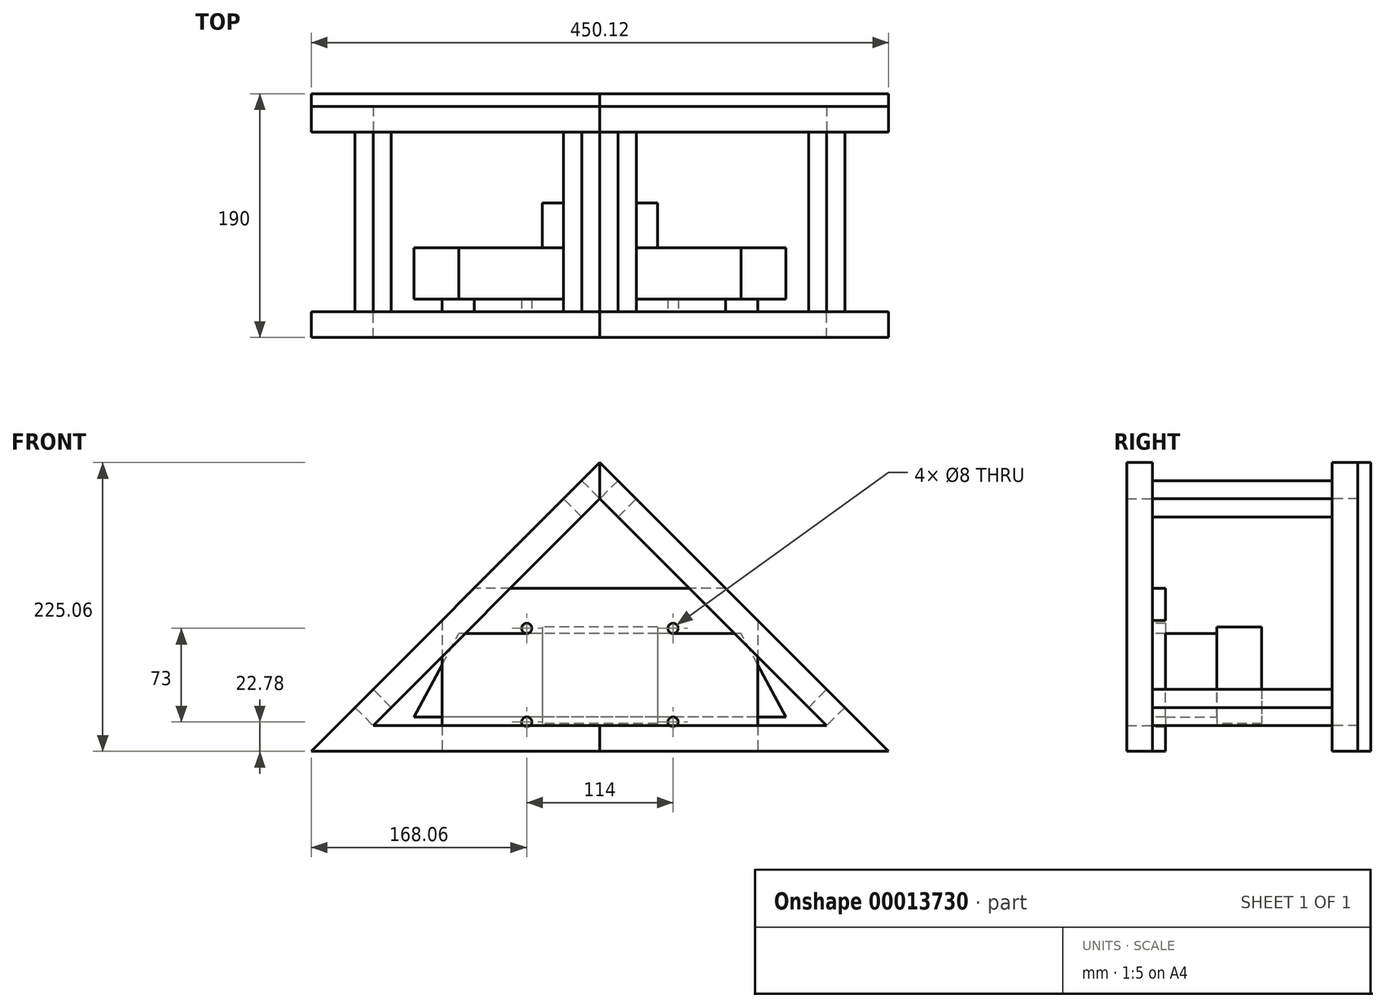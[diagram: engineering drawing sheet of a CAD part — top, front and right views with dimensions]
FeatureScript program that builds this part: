
annotation { "Feature Type Name" : "Feature", "Feature Type Description" : "" }
export const myFeature = defineFeature(function(context is Context, id is Id, definition is map)
    precondition{}
    {
        {
            var Q0;
            Q0=qCreatedBy(makeId("Front.planeOp"),FACE);
            var sketch = newSketch(context, id + "F0", { "sketchPlane" : qUnion([Q0])});
            skLineSegment(sketch, "E0", {"start": v(0, 0) * mm, "end": v(-145, 0) * mm});
            skLineSegment(sketch, "E1", {"start": v(-145, 0) * mm, "end": v(-110, 65) * mm});
            skLineSegment(sketch, "E2", {"start": v(-110, 65) * mm, "end": v(0, 65) * mm});
            skLineSegment(sketch, "E3", {"start": v(0, 65) * mm, "end": v(0, 0) * mm, "construction": true});
            skLineSegment(sketch, "E4.0.MirrorCS", {"start": v(110, 65) * mm, "end": v(0, 65) * mm});
            skLineSegment(sketch, "E5.0.MirrorCS", {"start": v(145, 0) * mm, "end": v(110, 65) * mm});
            skLineSegment(sketch, "E6.0.MirrorCS", {"start": v(0, 0) * mm, "end": v(145, 0) * mm});
            skSolve(sketch);
        }
        {
            var Q0;
            Q0 = qSketchRegion(id + "F0", true);
            extrude(context, id + "F1", {"entities" : qUnion([Q0]), "depth" : 40 * mm});
        }
        {
            var Q0;
            Q0=qCreatedBy(makeId("Front.planeOp"),FACE);
            var sketch = newSketch(context, id + "F2", { "sketchPlane" : qUnion([Q0])});
            skLineSegment(sketch, "E7.bottom", {"start": v(45, 70) * mm, "end": v(-45, 70) * mm});
            skLineSegment(sketch, "E7.top", {"start": v(45, -5) * mm, "end": v(-45, -5) * mm});
            skLineSegment(sketch, "E7.left", {"start": v(45, 70) * mm, "end": v(45, -5) * mm});
            skLineSegment(sketch, "E7.right", {"start": v(-45, 70) * mm, "end": v(-45, -5) * mm});
            skSolve(sketch);
        }
        {
            var Q0;
            Q0 = qSketchRegion(id + "F2", true);
            extrude(context, id + "F3", {"entities" : qUnion([Q0]), "operationType" : NewBodyOperationType.ADD, "oppositeDirection" : true, "depth" : 35 * mm});
        }
        {
            var Q0;
            Q0=qCreatedBy(makeId("Front.planeOp"),FACE);
            var sketch = newSketch(context, id + "F4", { "sketchPlane" : qUnion([Q0])});
            skLineSegment(sketch, "E8", {"start": v(0, -182.57) * mm, "end": v(0, 158.85) * mm, "construction": true});
            skLineSegment(sketch, "E9", {"start": v(0, 170) * mm, "end": v(-176.78, -6.78) * mm});
            skLineSegment(sketch, "E10", {"start": v(-14.14, 184.14) * mm, "end": v(-190.92, 7.37) * mm});
            skLineSegment(sketch, "E11", {"start": v(0, 170) * mm, "end": v(-14.14, 184.14) * mm});
            skLineSegment(sketch, "E12", {"start": v(-176.78, -6.78) * mm, "end": v(-190.92, 7.37) * mm});
            skLineSegment(sketch, "E13.bottom", {"start": v(-176.78, -6.78) * mm, "end": v(0, -6.78) * mm});
            skLineSegment(sketch, "E13.top", {"start": v(-176.78, -26.78) * mm, "end": v(0, -26.78) * mm});
            skLineSegment(sketch, "E13.left", {"start": v(-176.78, -6.78) * mm, "end": v(-176.78, -26.78) * mm});
            skLineSegment(sketch, "E13.right", {"start": v(0, -6.78) * mm, "end": v(0, -26.78) * mm});
            skLineSegment(sketch, "E14", {"start": v(-176.78, -26.78) * mm, "end": v(-225.06, -26.78) * mm});
            skLineSegment(sketch, "E15", {"start": v(-225.06, -26.78) * mm, "end": v(-190.92, 7.37) * mm});
            skLineSegment(sketch, "E16", {"start": v(-225.06, -26.78) * mm, "end": v(-176.78, -6.78) * mm});
            skLineSegment(sketch, "E17", {"start": v(-14.14, 184.14) * mm, "end": v(0, 198.28) * mm});
            skLineSegment(sketch, "E18", {"start": v(0, 198.28) * mm, "end": v(0, 170) * mm});
            skSolve(sketch);
        }
        {
            var Q0;
            Q0 = qSketchRegion(id + "F4", true);
            extrude(context, id + "F5", {"entities" : qUnion([Q0]), "operationType" : NewBodyOperationType.ADD, "oppositeDirection" : true, "depth" : 110 * mm, "hasSecondDirection" : true, "secondDirectionOppositeDirection" : true, "secondDirectionDepth" : 90 * mm});
        }
        {
            var Q0;
            Q0=makeQuery(id+"F1.opExtrude","CAP_FACE",FACE,{"disambiguationData":[OSD([sQuery(id+"F0.wireOp",EDGE,"E0"),sQuery(id+"F0.wireOp",EDGE,"E1"),sQuery(id+"F0.wireOp",EDGE,"E2"),sQuery(id+"F0.wireOp",EDGE,"E4.0.MirrorCS"),sQuery(id+"F0.wireOp",EDGE,"E5.0.MirrorCS"),sQuery(id+"F0.wireOp",EDGE,"E6.0.MirrorCS")])],"isStart":false});
            cPlane(context, id + "F6", {"entities" : qUnion([Q0]), "cplaneType" : CPlaneType.OFFSET, "offset" : 10 * mm, "width" : 150 * mm, "height" : 150 * mm});
        }
        {
            var Q0;
            Q0=qCreatedBy(id+"F6.planeOp",FACE);
            var sketch = newSketch(context, id + "F7", { "sketchPlane" : qUnion([Q0])});
            skLineSegment(sketch, "E19", {"start": v(0, -115.22) * mm, "end": v(0, 226.2) * mm, "construction": true});
            skLineSegment(sketch, "E20", {"start": v(0, 170) * mm, "end": v(-176.78, -6.78) * mm});
            skLineSegment(sketch, "E21", {"start": v(-14.14, 184.14) * mm, "end": v(-190.92, 7.37) * mm});
            skLineSegment(sketch, "E22", {"start": v(0, 170) * mm, "end": v(-14.14, 184.14) * mm});
            skLineSegment(sketch, "E23", {"start": v(-176.78, -6.78) * mm, "end": v(-190.92, 7.37) * mm});
            skLineSegment(sketch, "E24.bottom", {"start": v(-176.78, -6.78) * mm, "end": v(0, -6.78) * mm});
            skLineSegment(sketch, "E24.top", {"start": v(-176.78, -26.78) * mm, "end": v(0, -26.78) * mm});
            skLineSegment(sketch, "E24.left", {"start": v(-176.78, -6.78) * mm, "end": v(-176.78, -26.78) * mm});
            skLineSegment(sketch, "E24.right", {"start": v(0, -6.78) * mm, "end": v(0, -26.78) * mm});
            skLineSegment(sketch, "E25", {"start": v(-176.78, -26.78) * mm, "end": v(-225.06, -26.78) * mm});
            skLineSegment(sketch, "E26", {"start": v(-225.06, -26.78) * mm, "end": v(-190.92, 7.37) * mm});
            skLineSegment(sketch, "E27", {"start": v(-225.06, -26.78) * mm, "end": v(-176.78, -6.78) * mm});
            skLineSegment(sketch, "E28", {"start": v(-14.14, 184.14) * mm, "end": v(0, 198.28) * mm});
            skLineSegment(sketch, "E29", {"start": v(0, 198.28) * mm, "end": v(0, 170) * mm});
            skSolve(sketch);
        }
        {
            var Q0;
            Q0 = qSketchRegion(id + "F7", true);
            extrude(context, id + "F8", {"entities" : qUnion([Q0]), "operationType" : NewBodyOperationType.ADD, "depth" : 20 * mm});
        }
        {
            var Q0;
            Q0=makeQuery(id+"F8.opExtrude","SWEPT_BODY",BODY,{"disambiguationData":[OSD([sQuery(id+"F7.wireOp",EDGE,"E20"),sQuery(id+"F7.wireOp",EDGE,"E21"),sQuery(id+"F7.wireOp",EDGE,"E24.bottom"),sQuery(id+"F7.wireOp",EDGE,"E24.top"),sQuery(id+"F7.wireOp",EDGE,"E24.right"),sQuery(id+"F7.wireOp",EDGE,"E25"),sQuery(id+"F7.wireOp",EDGE,"E26"),sQuery(id+"F7.wireOp",EDGE,"E28"),sQuery(id+"F7.wireOp",EDGE,"E29")])]});
            var Q1;
            Q1=makeQuery(id+"F5.opExtrude","SWEPT_BODY",BODY,{"disambiguationData":[OSD([sQuery(id+"F4.wireOp",EDGE,"E9"),sQuery(id+"F4.wireOp",EDGE,"E10"),sQuery(id+"F4.wireOp",EDGE,"E13.bottom"),sQuery(id+"F4.wireOp",EDGE,"E13.top"),sQuery(id+"F4.wireOp",EDGE,"E13.right"),sQuery(id+"F4.wireOp",EDGE,"E14"),sQuery(id+"F4.wireOp",EDGE,"E15"),sQuery(id+"F4.wireOp",EDGE,"E17"),sQuery(id+"F4.wireOp",EDGE,"E18")])]});
            var Q2;
            Q2=qCreatedBy(makeId("Right.planeOp"),FACE);
            mirror(context, id + "F9", {"operationType" : NewBodyOperationType.ADD, "entities" : qUnion([Q0, Q1]), "mirrorPlane" : qUnion([Q2])});
        }
        {
            var Q0;
            {var subQ0=makeQuery(id+"F8.opExtrude","CAP_FACE",FACE,{"disambiguationData":[OSD([sQuery(id+"F7.wireOp",EDGE,"E20"),sQuery(id+"F7.wireOp",EDGE,"E21"),sQuery(id+"F7.wireOp",EDGE,"E24.bottom"),sQuery(id+"F7.wireOp",EDGE,"E24.top"),sQuery(id+"F7.wireOp",EDGE,"E24.right"),sQuery(id+"F7.wireOp",EDGE,"E25"),sQuery(id+"F7.wireOp",EDGE,"E26"),sQuery(id+"F7.wireOp",EDGE,"E28"),sQuery(id+"F7.wireOp",EDGE,"E29")])],"isStart":true});Q0=makeQuery(id+"F9.boolean.opBoolean","MERGE",FACE,{"derivedFrom":[subQ0,makeQuery(id+"F9.opPattern","COPY",FACE,{"derivedFrom":subQ0,"instanceName":"1"})]});}
            var sketch = newSketch(context, id + "F10", { "sketchPlane" : qUnion([Q0])});
            skLineSegment(sketch, "E30", {"start": v(-98.05, 100.23) * mm, "end": v(-123.08, 75.2) * mm});
            skLineSegment(sketch, "E31", {"start": v(-123.08, -26.78) * mm, "end": v(123.08, -26.78) * mm});
            skLineSegment(sketch, "E32", {"start": v(123.08, 75.2) * mm, "end": v(98.05, 100.23) * mm});
            skLineSegment(sketch, "E33", {"start": v(0, 198.28) * mm, "end": v(0, 32.3) * mm, "construction": true});
            skCircle(sketch, "E34", {"center": v(-57, 69) * mm, "radius": 4 * mm});
            skCircle(sketch, "E35.0.MirrorC", {"center": v(57, 69) * mm, "radius": 4 * mm});
            skCircle(sketch, "E36", {"center": v(-57, -4) * mm, "radius": 4 * mm});
            skCircle(sketch, "E37.0.MirrorC", {"center": v(57, -4) * mm, "radius": 4 * mm});
            skLineSegment(sketch, "E38", {"start": v(-98.05, 100.23) * mm, "end": v(98.05, 100.23) * mm});
            skLineSegment(sketch, "E39", {"start": v(-123.08, 75.2) * mm, "end": v(-123.08, -26.78) * mm});
            skLineSegment(sketch, "E40.0.MirrorCS", {"start": v(123.08, 75.2) * mm, "end": v(123.08, -26.78) * mm});
            skSolve(sketch);
        }
        {
            var Q0;
            Q0 = qSketchRegion(id + "F10", true);
            extrude(context, id + "F11", {"entities" : qUnion([Q0]), "depth" : 10 * mm});
        }
        {
            var Q0;
            {var subQ0=makeQuery(id+"F5.opExtrude","CAP_FACE",FACE,{"disambiguationData":[OSD([sQuery(id+"F4.wireOp",EDGE,"E9"),sQuery(id+"F4.wireOp",EDGE,"E10"),sQuery(id+"F4.wireOp",EDGE,"E13.bottom"),sQuery(id+"F4.wireOp",EDGE,"E13.top"),sQuery(id+"F4.wireOp",EDGE,"E13.right"),sQuery(id+"F4.wireOp",EDGE,"E14"),sQuery(id+"F4.wireOp",EDGE,"E15"),sQuery(id+"F4.wireOp",EDGE,"E17"),sQuery(id+"F4.wireOp",EDGE,"E18")])],"isStart":false});Q0=makeQuery(id+"F9.boolean.opBoolean","MERGE",FACE,{"derivedFrom":[subQ0,makeQuery(id+"F9.opPattern","COPY",FACE,{"derivedFrom":subQ0,"instanceName":"1"})]});}
            var sketch = newSketch(context, id + "F12", { "sketchPlane" : qUnion([Q0])});
            skLineSegment(sketch, "E41", {"start": v(0, 198.28) * mm, "end": v(-225.06, -26.78) * mm});
            skLineSegment(sketch, "E42", {"start": v(-225.06, -26.78) * mm, "end": v(225.06, -26.78) * mm});
            skLineSegment(sketch, "E43", {"start": v(225.06, -26.78) * mm, "end": v(0, 198.28) * mm});
            skSolve(sketch);
        }
        {
            var Q0;
            Q0 = qSketchRegion(id + "F12", true);
            extrude(context, id + "F13", {"entities" : qUnion([Q0]), "depth" : 10 * mm});
        }
        {
            var Q0;
            {var subQ0=makeQuery(id+"F8.opExtrude","CAP_FACE",FACE,{"disambiguationData":[OSD([sQuery(id+"F7.wireOp",EDGE,"E20"),sQuery(id+"F7.wireOp",EDGE,"E21"),sQuery(id+"F7.wireOp",EDGE,"E24.bottom"),sQuery(id+"F7.wireOp",EDGE,"E24.top"),sQuery(id+"F7.wireOp",EDGE,"E24.right"),sQuery(id+"F7.wireOp",EDGE,"E25"),sQuery(id+"F7.wireOp",EDGE,"E26"),sQuery(id+"F7.wireOp",EDGE,"E28"),sQuery(id+"F7.wireOp",EDGE,"E29")])],"isStart":true});Q0=makeQuery(id+"F9.boolean.opBoolean","MERGE",FACE,{"derivedFrom":[subQ0,makeQuery(id+"F9.opPattern","COPY",FACE,{"derivedFrom":subQ0,"instanceName":"1"})]});}
            var sketch = newSketch(context, id + "F14", { "sketchPlane" : qUnion([Q0])});
            skLineSegment(sketch, "E44", {"start": v(0, 170) * mm, "end": v(-14.14, 184.14) * mm});
            skLineSegment(sketch, "E45", {"start": v(-14.14, 184.14) * mm, "end": v(-28.28, 170) * mm});
            skLineSegment(sketch, "E46", {"start": v(-28.28, 170) * mm, "end": v(-14.14, 155.86) * mm});
            skLineSegment(sketch, "E47", {"start": v(-14.14, 155.86) * mm, "end": v(0, 170) * mm});
            skLineSegment(sketch, "E48", {"start": v(-176.78, -6.78) * mm, "end": v(-190.92, 7.37) * mm});
            skLineSegment(sketch, "E49", {"start": v(-190.92, 7.37) * mm, "end": v(-176.78, 21.5) * mm});
            skLineSegment(sketch, "E50", {"start": v(-176.78, 21.5) * mm, "end": v(-162.63, 7.37) * mm});
            skLineSegment(sketch, "E51", {"start": v(-162.63, 7.37) * mm, "end": v(-176.78, -6.78) * mm});
            skLineSegment(sketch, "E52", {"start": v(0, 198.28) * mm, "end": v(0, 145.24) * mm, "construction": true});
            skLineSegment(sketch, "E53.0.MirrorCS", {"start": v(0, 170) * mm, "end": v(14.14, 184.14) * mm});
            skLineSegment(sketch, "E54.0.MirrorCS", {"start": v(14.14, 184.14) * mm, "end": v(28.28, 170) * mm});
            skLineSegment(sketch, "E55.0.MirrorCS", {"start": v(28.28, 170) * mm, "end": v(14.14, 155.86) * mm});
            skLineSegment(sketch, "E56.0.MirrorCS", {"start": v(14.14, 155.86) * mm, "end": v(0, 170) * mm});
            skLineSegment(sketch, "E57.0.MirrorCS", {"start": v(190.92, 7.37) * mm, "end": v(176.78, 21.5) * mm});
            skLineSegment(sketch, "E58.0.MirrorCS", {"start": v(176.78, -6.78) * mm, "end": v(190.92, 7.37) * mm});
            skLineSegment(sketch, "E59.0.MirrorCS", {"start": v(176.78, 21.5) * mm, "end": v(162.63, 7.37) * mm});
            skLineSegment(sketch, "E60.0.MirrorCS", {"start": v(162.63, 7.37) * mm, "end": v(176.78, -6.78) * mm});
            skSolve(sketch);
        }
        {
            var Q0;
            Q0 = qSketchRegion(id + "F14", true);
            var Q1;
            {var subQ0=makeQuery(id+"F5.opExtrude","CAP_FACE",FACE,{"disambiguationData":[OSD([sQuery(id+"F4.wireOp",EDGE,"E9"),sQuery(id+"F4.wireOp",EDGE,"E10"),sQuery(id+"F4.wireOp",EDGE,"E13.bottom"),sQuery(id+"F4.wireOp",EDGE,"E13.top"),sQuery(id+"F4.wireOp",EDGE,"E13.right"),sQuery(id+"F4.wireOp",EDGE,"E14"),sQuery(id+"F4.wireOp",EDGE,"E15"),sQuery(id+"F4.wireOp",EDGE,"E17"),sQuery(id+"F4.wireOp",EDGE,"E18")])],"isStart":true});Q1=makeQuery(id+"F9.boolean.opBoolean","MERGE",FACE,{"derivedFrom":[subQ0,makeQuery(id+"F9.opPattern","COPY",FACE,{"derivedFrom":subQ0,"instanceName":"1"})]});}
            extrude(context, id + "F15", {"entities" : qUnion([Q0]), "endBound" : BoundingType.UP_TO_SURFACE, "endBoundEntityFace" : qUnion([Q1]), "depth" : 25 * mm});
        }
    });
